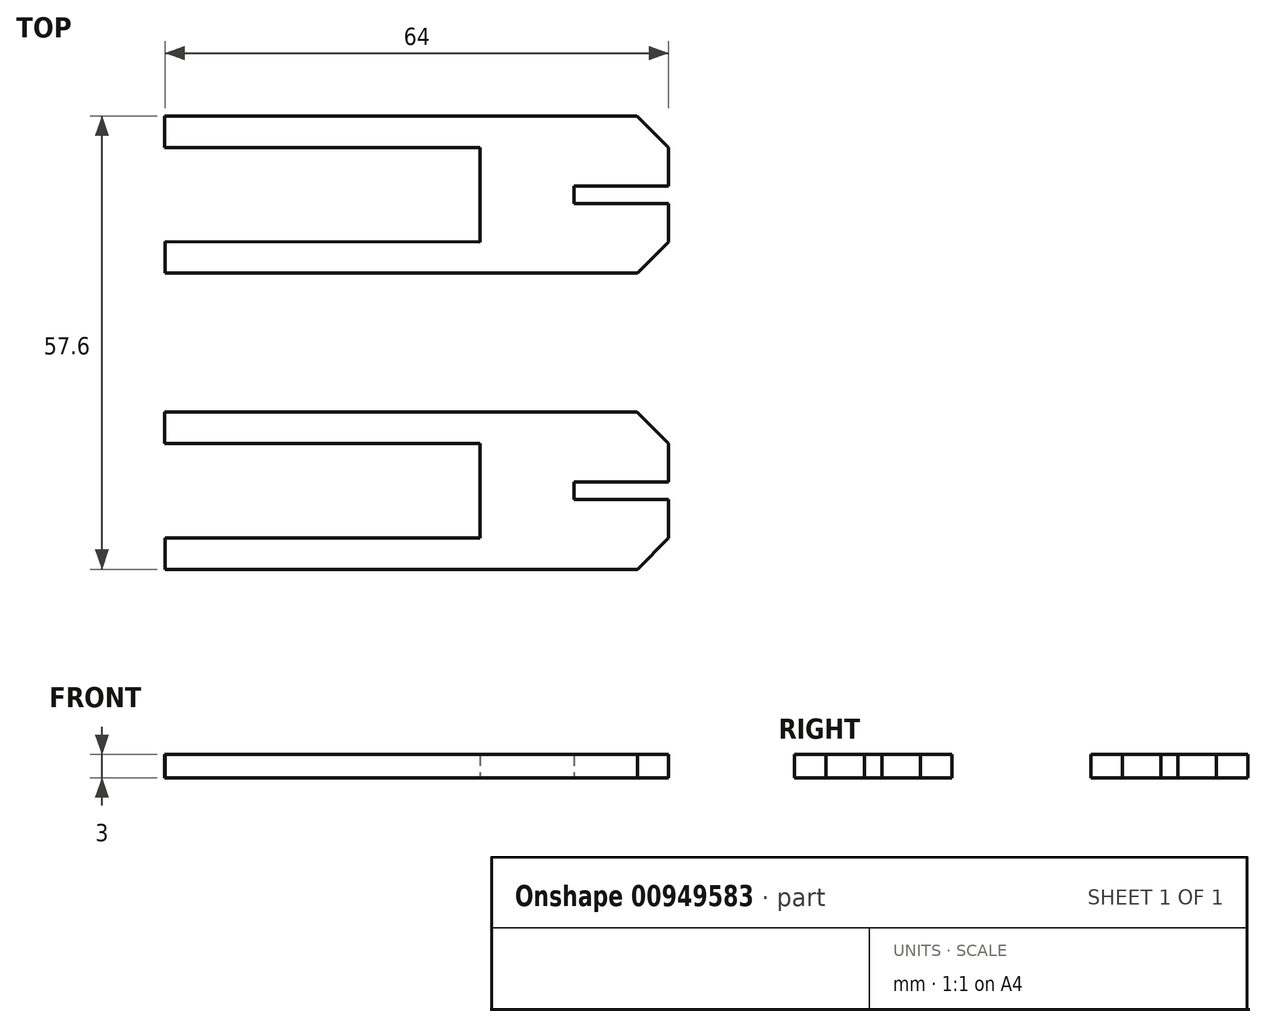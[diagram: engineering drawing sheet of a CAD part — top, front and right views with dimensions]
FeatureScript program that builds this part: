
annotation { "Feature Type Name" : "Feature", "Feature Type Description" : "" }
export const myFeature = defineFeature(function(context is Context, id is Id, definition is map)
    precondition{}
    {
        {
            var Q0;
            Q0=qCreatedBy(makeId("Top.planeOp"),FACE);
            var sketch = newSketch(context, id + "F0", { "sketchPlane" : qUnion([Q0])});
            skLineSegment(sketch, "E0", {"start": v(-58.05, 15.4) * mm, "end": v(-58.05, 11.38) * mm});
            skLineSegment(sketch, "E1", {"start": v(-58.05, 11.38) * mm, "end": v(1.96, 11.38) * mm});
            skLineSegment(sketch, "E2", {"start": v(1.96, 11.38) * mm, "end": v(5.94, 15.36) * mm});
            skLineSegment(sketch, "E3", {"start": v(5.94, 15.36) * mm, "end": v(5.94, 20.26) * mm});
            skLineSegment(sketch, "E4", {"start": v(5.94, 20.26) * mm, "end": v(-6.06, 20.26) * mm});
            skLineSegment(sketch, "E5", {"start": v(-6.06, 20.26) * mm, "end": v(-6.06, 22.46) * mm});
            skLineSegment(sketch, "E6", {"start": v(-6.06, 22.46) * mm, "end": v(5.94, 22.46) * mm});
            skLineSegment(sketch, "E7", {"start": v(5.94, 22.46) * mm, "end": v(5.94, 27.36) * mm});
            skLineSegment(sketch, "E8", {"start": v(5.94, 27.36) * mm, "end": v(1.94, 31.36) * mm});
            skLineSegment(sketch, "E9", {"start": v(1.94, 31.36) * mm, "end": v(-58.06, 31.36) * mm});
            skLineSegment(sketch, "E10", {"start": v(-58.06, 31.36) * mm, "end": v(-58.06, 27.36) * mm});
            skLineSegment(sketch, "E11", {"start": v(-58.06, 27.36) * mm, "end": v(-18.06, 27.36) * mm});
            skLineSegment(sketch, "E12", {"start": v(-18.06, 27.36) * mm, "end": v(-18.06, 15.36) * mm});
            skLineSegment(sketch, "E13", {"start": v(-18.06, 15.36) * mm, "end": v(-58.05, 15.4) * mm});
            skLineSegment(sketch, "E14", {"start": v(-58.05, -22.22) * mm, "end": v(-58.05, -26.24) * mm});
            skLineSegment(sketch, "E15", {"start": v(-58.05, -26.24) * mm, "end": v(1.96, -26.24) * mm});
            skLineSegment(sketch, "E16", {"start": v(1.96, -26.24) * mm, "end": v(5.94, -22.26) * mm});
            skLineSegment(sketch, "E17", {"start": v(5.94, -22.26) * mm, "end": v(5.94, -17.37) * mm});
            skLineSegment(sketch, "E18", {"start": v(5.94, -17.37) * mm, "end": v(-6.06, -17.37) * mm});
            skLineSegment(sketch, "E19", {"start": v(-6.06, -17.37) * mm, "end": v(-6.06, -15.17) * mm});
            skLineSegment(sketch, "E20", {"start": v(-6.06, -15.17) * mm, "end": v(5.94, -15.17) * mm});
            skLineSegment(sketch, "E21", {"start": v(5.94, -15.17) * mm, "end": v(5.94, -10.27) * mm});
            skLineSegment(sketch, "E22", {"start": v(5.94, -10.27) * mm, "end": v(1.94, -6.27) * mm});
            skLineSegment(sketch, "E23", {"start": v(1.94, -6.27) * mm, "end": v(-58.06, -6.27) * mm});
            skLineSegment(sketch, "E24", {"start": v(-58.06, -6.27) * mm, "end": v(-58.06, -10.27) * mm});
            skLineSegment(sketch, "E25", {"start": v(-58.06, -10.27) * mm, "end": v(-18.06, -10.27) * mm});
            skLineSegment(sketch, "E26", {"start": v(-18.06, -10.27) * mm, "end": v(-18.06, -22.26) * mm});
            skLineSegment(sketch, "E27", {"start": v(-18.06, -22.26) * mm, "end": v(-58.05, -22.22) * mm});
            skSolve(sketch);
        }
        {
            var Q0;
            Q0=makeQuery(id+"F0.imprint","IMPRINT",FACE,{"disambiguationData":[TD([[makeQuery(id+"F0.imprint","IMPRINT",EDGE,{"derivedFrom":sQuery(id+"F0.wireOp",EDGE,"E0")}),1.0]])]});
            var Q1;
            Q1=makeQuery(id+"F0.imprint","IMPRINT",FACE,{"disambiguationData":[TD([[makeQuery(id+"F0.imprint","IMPRINT",EDGE,{"derivedFrom":sQuery(id+"F0.wireOp",EDGE,"E14")}),1.0]])]});
            extrude(context, id + "F1", {"entities" : qUnion([Q0, Q1]), "depth" : 3 * mm, "offsetDistance" : 25 * mm});
        }
    });
